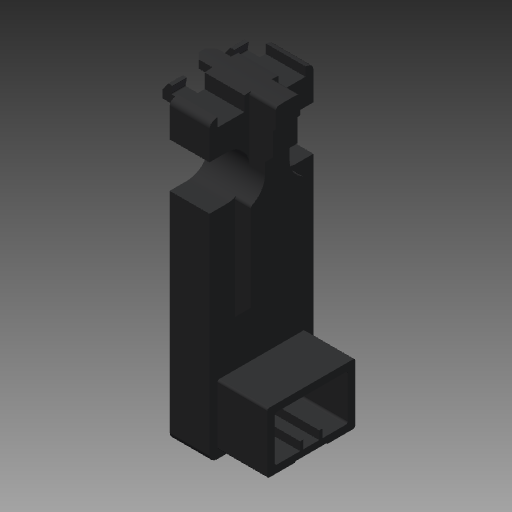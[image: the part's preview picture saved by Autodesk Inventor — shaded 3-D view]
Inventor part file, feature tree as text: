
AUTODESK INVENTOR PART (.ipt)
format: ipt  version: 2017.1 (Build 211199000, 199)  size: 274,432 bytes
history: native  units: mm
features: extrude x14, other x14, sketch x14
ambient origin geometry x8: Origin, YZ Plane, XZ Plane, XY Plane, X Axis, Y Axis, Z Axis, Center Point
bodies: Solid1 (feature_tree)
feature tree (42):
  extrude  "Extrusion1"  Depth=8.45mm TaperAngle=0.0deg
  extrude  "Extrusion2"  Depth=8.45mm TaperAngle=0.0deg
  extrude  "Extrusion3"  Depth=2.5mm TaperAngle=0.0deg
  extrude  "Extrusion4"  Depth=10.0mm TaperAngle=0.0deg
  extrude  "Extrusion5"  Depth=7.2mm TaperAngle=0.0deg
  extrude  "Extrusion6"  Depth=1.85mm TaperAngle=0.0deg
  extrude  "Extrusion7"  Depth=0.85mm TaperAngle=0.0deg
  extrude  "Extrusion8"  [1 undecoded]
  extrude  "Extrusion9"  [1 undecoded]
  extrude  "Extrusion10"  [1 undecoded]
  extrude  "Extrusion11"  [1 undecoded]
  extrude  "Extrusion12"  [1 undecoded]
  extrude  "Extrusion13"  [1 undecoded]
  extrude  "Extrusion14"  [1 undecoded]
  other  "NEBV_XY"
  other  "NEBV_YZ"
  other  "NEBV_ZX"
  other  "NEBV_X"
  other  "NEBV_Y"
  other  "NEBV_Z"
  other  "NEBV_Center"
  other  "VAVE_XY"
  other  "VAVE_YZ"
  other  "VAVE_ZX"
  other  "VAVE_X"
  other  "VAVE_Y"
  other  "VAVE_Z"
  other  "VAVE_Center"
  sketch  "Sketch_1"  dims[d0=8.45mm d1=0.0mm d2=8.45mm d3=0.0mm]
  sketch  "Sketch_2"  dims[d4=8.45mm d5=0.0mm d6=8.45mm d7=0.0mm]
  sketch  "Sketch_3"  dims[d8=8.45mm d9=0.0mm d10=2.5mm d11=0.0mm]
  sketch  "Sketch_4"  dims[d12=6.0mm d13=0.0mm d14=10.0mm d15=0.0mm]
  sketch  "Sketch_5"  dims[d16=3.0mm d17=0.0mm d18=7.2mm d19=0.0mm]
  sketch  "Sketch_7"  dims[d24=30.0mm d25=0.0mm d26=0.85mm d27=0.0mm]
  sketch  "Sketch_8"
  sketch  "Sketch_6"  dims[d20=30.0mm d21=0.0mm d22=1.85mm d23=0.0mm]
  sketch  "Sketch_9"
  sketch  "Sketch_13"
  sketch  "Sketch_14"
  sketch  "Sketch_11"
  sketch  "Sketch_10"
  sketch  "Sketch_12"
note: 7 required parameter values undecoded (feature->parameter linkage not recoverable at this tier; creation-order binding heuristic only, values carry confidence <= 0.55)
